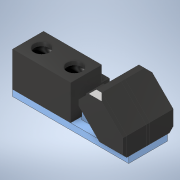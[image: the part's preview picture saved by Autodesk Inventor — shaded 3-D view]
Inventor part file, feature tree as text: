
AUTODESK INVENTOR PART (.ipt)
format: ipt  version: 2020 (Build 240168000, 168)  size: 392,192 bytes
history: native  units: mm
features: sketch x11, extrude x9, plane x4, chamfer x3, mirror x2, other x1, revolve x1
ambient origin geometry x8: Origin, YZ Plane, XZ Plane, XY Plane, X Axis, Y Axis, Z Axis, Center Point
bodies: Solid2 (feature_tree), Solid3 (feature_tree), Solid4 (feature_tree), Solid6 (feature_tree)
feature tree (31):
  other  "Bryła1"
  extrude  "Wyciągnięcie proste1"  Depth=15.0mm
  extrude  "Wyciągnięcie proste2"  Depth=7.5mm
  extrude  "Wyciągnięcie proste3"  Depth=8.0mm
  extrude  "Extrusion4"  Depth=4.0mm
  extrude  "Extrusion5"  Depth=4.0mm
  extrude  "Extrusion7"  Depth=4.0mm
  plane  "Work Plane1"
  plane  "Work Plane2"
  plane  "Work Plane3"
  plane  "Work Plane4"
  sketch  "Sketch9"  dims[d10=3.5mm d11=4.0mm]
  revolve  "Revolution1"  [1 undecoded]
  extrude  "Extrusion8"  Depth=30.0mm
  mirror  "Mirror1"
  chamfer  "Chamfer1"  Distance=3.5mm
  extrude  "Extrusion11"  Depth=5.7mm
  mirror  "Mirror4"
  extrude  "Extrusion12"  Depth=2.15mm
  chamfer  "Chamfer2"  Distance=0.75mm
  chamfer  "Chamfer3"  Distance=4.8mm
  sketch  "Szkic1"
  sketch  "Szkic2"
  sketch  "Szkic3"
  sketch  "Sketch4"  dims[d0=10.0mm d1=15.0mm]
  sketch  "Sketch5"  dims[d2=5.0mm d3=7.5mm]
  sketch  "Sketch7"  dims[d4=5.0mm d5=0.0mm d6=8.0mm]
  sketch  "Sketch8"  dims[d7=4.0mm d8=0.0mm d9=4.0mm]
  sketch  "Sketch12"  dims[d14=4.0mm d15=1.0mm d16=0.0mm]
  sketch  "Sketch13"  dims[d17=1.6mm d18=0.0mm d19=30.0mm d20=3.5mm d21=5.7mm d22=2.15mm d23=0.75mm d24=4.8mm d25=0.0mm d32=4.4mm d33=0.65mm d34=2.4mm d35=0.5mm d36=1.0mm d37=0.0mm d38=-2.0mm d39=5.0mm d40=6.5mm d41=45.0deg d44=5.0mm d45=-1.0mm d46=-1.0mm d47=0.4mm d48=0.0mm d49=1.0mm d50=3.054326mm d51=6.108652mm d53=3.0mm d54=1.0mm d55=1.0mm d56=0.0mm d57=0.0mm d58=0.0mm d59=0.0mm d60=0.0mm d62=0.0mm d64=0.117798mm d65=0.0mm d66=0.0mm d67=90.0deg d68=5.0mm d69=6.5mm d71=5.0mm d72=1.0mm d73=1.0mm d74=0.0mm d75=0.0mm d76=1.0mm d77=1.0mm d78=0.0mm d80=0.117798mm d81=0.0mm d83=5.0mm d84=0.0mm d86=-5.0mm d91=1.0mm d92=2.0mm d93=45.0deg d94=1.0mm d95=0.0mm d96=1.0mm d97=0.0mm d98=1.0mm d99=2.0mm d100=45.0deg d101=1.0mm d102=2.0mm d103=45.0deg d85=0.5mm d87=0.872665mm d88=0.5mm d89=0.872665mm]
  sketch  "Sketch10"  dims[d12=3.0mm d13=4.0mm]
note: 1 required parameter value undecoded (feature->parameter linkage not recoverable at this tier; creation-order binding heuristic only, values carry confidence <= 0.55)
